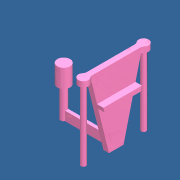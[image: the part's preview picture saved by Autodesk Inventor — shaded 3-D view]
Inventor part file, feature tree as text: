
AUTODESK INVENTOR PART (.ipt)
format: ipt  version: 2020 (Build 240168000, 168)  size: 186,368 bytes
history: native  units: mm
features: extrude x8, sketch x8, mirror x1, projected_geometry x1
ambient origin geometry x8: Origin, YZ Plane, XZ Plane, XY Plane, X Axis, Y Axis, Z Axis, Center Point
bodies: Solid1 (feature_tree)
feature tree (18):
  extrude  "Extrusion1"  Depth=33.0mm TaperAngle=0.0deg
  extrude  "Extrusion2"  Depth=20.0mm TaperAngle=0.0deg
  extrude  "Extrusion3"  Depth=10.0mm
  extrude  "Extrusion4"  Depth=3.5mm
  extrude  "Extrusion5"  Depth=77.0mm
  extrude  "Extrusion6"  Depth=6.0mm TaperAngle=0.0deg
  extrude  "Extrusion7"  Depth=33.0mm
  mirror  "Mirror1"
  extrude  "Extrusion8"  Depth=6.0mm TaperAngle=0.0deg
  sketch  "Sketch1"  dims[d0=7.0mm d1=33.0mm d2=0.0mm]
  sketch  "Sketch2"  dims[d3=14.0mm d4=20.0mm d5=0.0mm]
  sketch  "Sketch3"  dims[d6=57.5mm d7=10.0mm]
  sketch  "Sketch4"  dims[d8=3.5mm d9=0.0mm d10=8.0mm]
  sketch  "Sketch5"  dims[d11=27.0mm d12=77.0mm]
  projected_geometry  "Projected Loop1"
  sketch  "Sketch6"  dims[d13=6.0mm d14=0.0mm d15=6.0mm d16=0.0mm]
  sketch  "Sketch7"  dims[d17=11.0mm d18=33.0mm]
  sketch  "Sketch8"  dims[d19=3.0mm d20=6.0mm d21=0.0mm d22=5.5mm d23=77.0mm d24=0.0mm d27=30.0mm d28=7.0mm d29=0.0mm d30=5.0mm]
